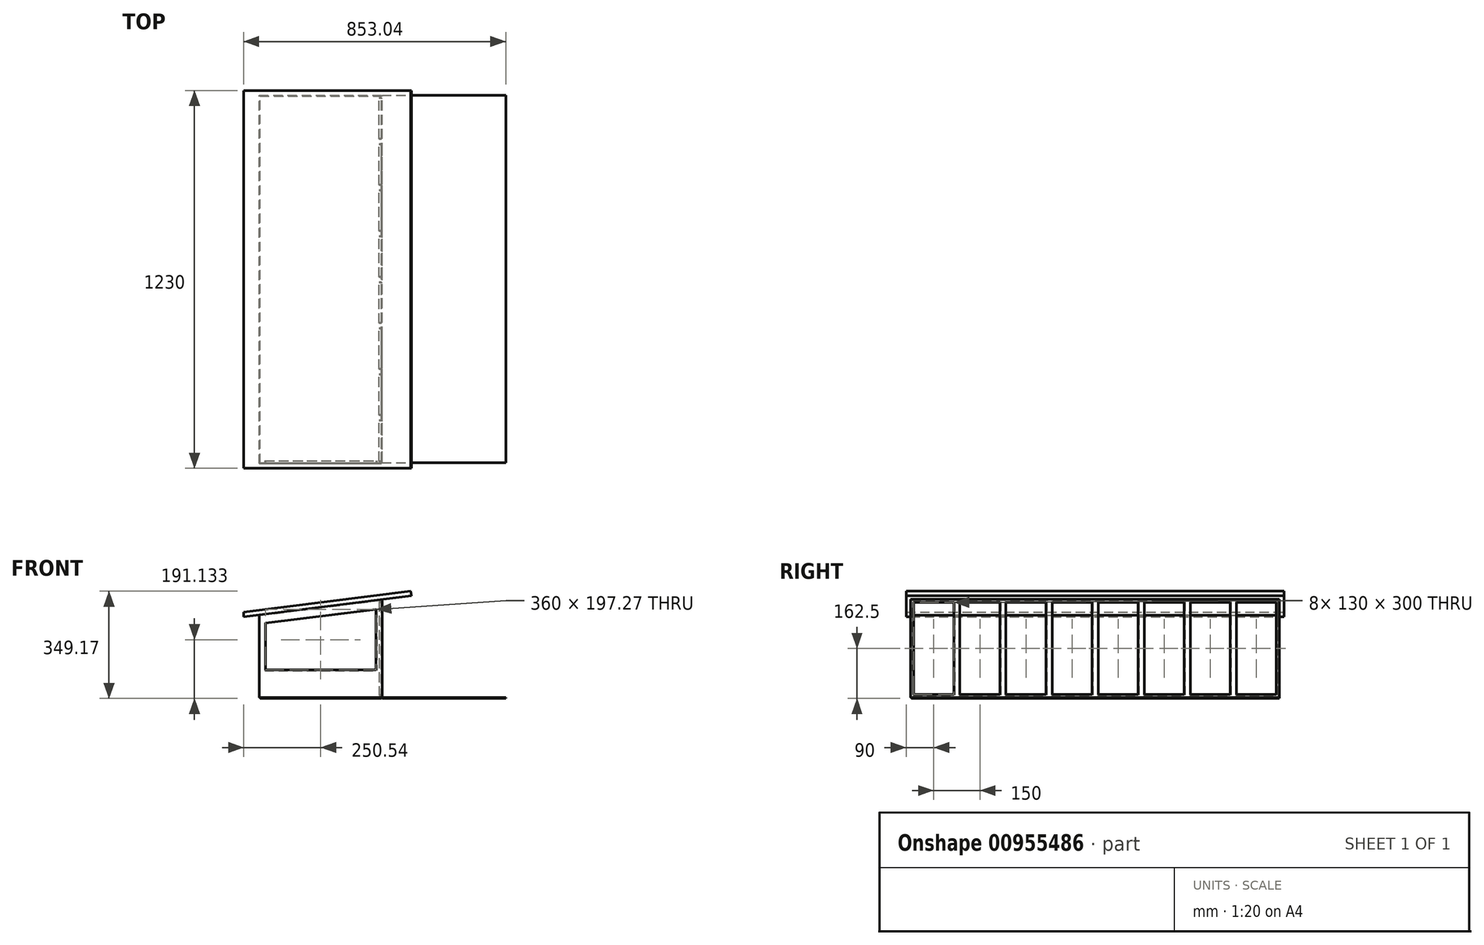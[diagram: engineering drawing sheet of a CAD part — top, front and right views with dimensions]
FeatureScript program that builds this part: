
annotation { "Feature Type Name" : "Feature", "Feature Type Description" : "" }
export const myFeature = defineFeature(function(context is Context, id is Id, definition is map)
    precondition{}
    {
        {
            var Q0;
            Q0=qCreatedBy(makeId("Front.planeOp"),FACE);
            var sketch = newSketch(context, id + "F0", { "sketchPlane" : qUnion([Q0])});
            skLineSegment(sketch, "E0", {"start": v(0, 0) * mm, "end": v(400, 0) * mm});
            skLineSegment(sketch, "E1", {"start": v(0, 0) * mm, "end": v(0, 270) * mm});
            skLineSegment(sketch, "E2", {"start": v(400, 0) * mm, "end": v(400, 320) * mm});
            skLineSegment(sketch, "E3", {"start": v(0, 270) * mm, "end": v(400, 320) * mm});
            skSolve(sketch);
        }
        {
            var Q0;
            Q0 = qSketchRegion(id + "F0", true);
            extrude(context, id + "F1", {"entities" : qUnion([Q0]), "depth" : 1200 * mm, "offsetDistance" : 25 * mm});
        }
        {
            var Q0;
            Q0=qCreatedBy(makeId("Front.planeOp"),FACE);
            var sketch = newSketch(context, id + "F2", { "sketchPlane" : qUnion([Q0])});
            skLineSegment(sketch, "E4", {"start": v(-50.54, 263.68) * mm, "end": v(-50.54, 278.68) * mm});
            skLineSegment(sketch, "E5", {"start": v(-50.54, 278.68) * mm, "end": v(493.37, 346.67) * mm});
            skLineSegment(sketch, "E6", {"start": v(493.37, 346.67) * mm, "end": v(495.22, 331.9) * mm});
            skLineSegment(sketch, "E7", {"start": v(-50.54, 263.68) * mm, "end": v(495.22, 331.9) * mm});
            skSolve(sketch);
        }
        {
            var Q0;
            Q0=makeQuery(id+"F2.imprint","IMPRINT",FACE,{"disambiguationData":[TD([[makeQuery(id+"F2.imprint","IMPRINT",EDGE,{"derivedFrom":sQuery(id+"F2.wireOp",EDGE,"E4")}),-1.0]])]});
            extrude(context, id + "F3", {"entities" : qUnion([Q0]), "depth" : 1215 * mm, "offsetDistance" : 25 * mm, "hasSecondDirection" : true, "secondDirectionOppositeDirection" : true, "secondDirectionDepth" : 15 * mm});
        }
        {
            var Q0;
            Q0=makeQuery(id+"F1.opExtrude","SWEPT_FACE",FACE,{"disambiguationData":[OSD([sQuery(id+"F0.wireOp",EDGE,"E2")])]});
            var sketch = newSketch(context, id + "F4", { "sketchPlane" : qUnion([Q0])});
            skLineSegment(sketch, "E8", {"start": v(-600, 320) * mm, "end": v(-600, 0) * mm});
            skLineSegment(sketch, "E9", {"start": v(-450, 320) * mm, "end": v(-450, 0) * mm});
            skLineSegment(sketch, "E10", {"start": v(-300, 320) * mm, "end": v(-300, 0) * mm});
            skLineSegment(sketch, "E11", {"start": v(-150, 320) * mm, "end": v(-150, 0) * mm});
            skLineSegment(sketch, "E12", {"start": v(-750, 320) * mm, "end": v(-750, 0) * mm});
            skLineSegment(sketch, "E13", {"start": v(-900, 320) * mm, "end": v(-900, 0) * mm});
            skLineSegment(sketch, "E14", {"start": v(-1050, 320) * mm, "end": v(-1050, 0) * mm});
            skLineSegment(sketch, "E15", {"start": v(-1200, 320) * mm, "end": v(-1050, 320) * mm});
            skLineSegment(sketch, "E16", {"start": v(-1050, 320) * mm, "end": v(-900, 320) * mm});
            skLineSegment(sketch, "E17", {"start": v(-900, 320) * mm, "end": v(-750, 320) * mm});
            skLineSegment(sketch, "E18", {"start": v(-750, 320) * mm, "end": v(-600, 320) * mm});
            skLineSegment(sketch, "E19", {"start": v(-600, 320) * mm, "end": v(-450, 320) * mm});
            skLineSegment(sketch, "E20", {"start": v(-450, 320) * mm, "end": v(-300, 320) * mm});
            skLineSegment(sketch, "E21", {"start": v(-300, 320) * mm, "end": v(-150, 320) * mm});
            skLineSegment(sketch, "E22", {"start": v(-150, 320) * mm, "end": v(0, 320) * mm});
            skLineSegment(sketch, "E23.bottom", {"start": v(-1190, 310) * mm, "end": v(-1060, 310) * mm});
            skLineSegment(sketch, "E23.top", {"start": v(-1190, 10) * mm, "end": v(-1060, 10) * mm});
            skLineSegment(sketch, "E23.left", {"start": v(-1190, 310) * mm, "end": v(-1190, 10) * mm});
            skLineSegment(sketch, "E23.right", {"start": v(-1060, 310) * mm, "end": v(-1060, 10) * mm});
            skLineSegment(sketch, "E24.bottom", {"start": v(-1040, 310) * mm, "end": v(-910, 310) * mm});
            skLineSegment(sketch, "E24.top", {"start": v(-1040, 10) * mm, "end": v(-910, 10) * mm});
            skLineSegment(sketch, "E24.left", {"start": v(-1040, 310) * mm, "end": v(-1040, 10) * mm});
            skLineSegment(sketch, "E24.right", {"start": v(-910, 310) * mm, "end": v(-910, 10) * mm});
            skLineSegment(sketch, "E25.bottom", {"start": v(-890, 310) * mm, "end": v(-760, 310) * mm});
            skLineSegment(sketch, "E25.top", {"start": v(-890, 10) * mm, "end": v(-760, 10) * mm});
            skLineSegment(sketch, "E25.left", {"start": v(-890, 310) * mm, "end": v(-890, 10) * mm});
            skLineSegment(sketch, "E25.right", {"start": v(-760, 310) * mm, "end": v(-760, 10) * mm});
            skLineSegment(sketch, "E26.bottom", {"start": v(-740, 310) * mm, "end": v(-610, 310) * mm});
            skLineSegment(sketch, "E26.top", {"start": v(-740, 10) * mm, "end": v(-610, 10) * mm});
            skLineSegment(sketch, "E26.left", {"start": v(-740, 310) * mm, "end": v(-740, 10) * mm});
            skLineSegment(sketch, "E26.right", {"start": v(-610, 310) * mm, "end": v(-610, 10) * mm});
            skLineSegment(sketch, "E27.bottom", {"start": v(-590, 310) * mm, "end": v(-460, 310) * mm});
            skLineSegment(sketch, "E27.top", {"start": v(-590, 10) * mm, "end": v(-460, 10) * mm});
            skLineSegment(sketch, "E27.left", {"start": v(-590, 310) * mm, "end": v(-590, 10) * mm});
            skLineSegment(sketch, "E27.right", {"start": v(-460, 310) * mm, "end": v(-460, 10) * mm});
            skLineSegment(sketch, "E28.bottom", {"start": v(-440, 310) * mm, "end": v(-310, 310) * mm});
            skLineSegment(sketch, "E28.top", {"start": v(-440, 10) * mm, "end": v(-310, 10) * mm});
            skLineSegment(sketch, "E28.left", {"start": v(-440, 310) * mm, "end": v(-440, 10) * mm});
            skLineSegment(sketch, "E28.right", {"start": v(-310, 310) * mm, "end": v(-310, 10) * mm});
            skLineSegment(sketch, "E29.bottom", {"start": v(-290, 310) * mm, "end": v(-160, 310) * mm});
            skLineSegment(sketch, "E29.top", {"start": v(-290, 10) * mm, "end": v(-160, 10) * mm});
            skLineSegment(sketch, "E29.left", {"start": v(-290, 310) * mm, "end": v(-290, 10) * mm});
            skLineSegment(sketch, "E29.right", {"start": v(-160, 310) * mm, "end": v(-160, 10) * mm});
            skLineSegment(sketch, "E30.bottom", {"start": v(-140, 310) * mm, "end": v(-10, 310) * mm});
            skLineSegment(sketch, "E30.top", {"start": v(-140, 10) * mm, "end": v(-10, 10) * mm});
            skLineSegment(sketch, "E30.left", {"start": v(-140, 310) * mm, "end": v(-140, 10) * mm});
            skLineSegment(sketch, "E30.right", {"start": v(-10, 310) * mm, "end": v(-10, 10) * mm});
            skSolve(sketch);
        }
        {
            var Q0;
            Q0=makeQuery(id+"F4.imprint","IMPRINT",FACE,{"disambiguationData":[TD([[makeQuery(id+"F4.imprint","IMPRINT",EDGE,{"derivedFrom":sQuery(id+"F4.wireOp",EDGE,"E23.bottom")}),-1.0]])]});
            var Q1;
            Q1=makeQuery(id+"F4.imprint","IMPRINT",FACE,{"disambiguationData":[TD([[makeQuery(id+"F4.imprint","IMPRINT",EDGE,{"derivedFrom":sQuery(id+"F4.wireOp",EDGE,"E24.bottom")}),-1.0]])]});
            var Q2;
            Q2=makeQuery(id+"F4.imprint","IMPRINT",FACE,{"disambiguationData":[TD([[makeQuery(id+"F4.imprint","IMPRINT",EDGE,{"derivedFrom":sQuery(id+"F4.wireOp",EDGE,"E25.bottom")}),-1.0]])]});
            var Q3;
            Q3=makeQuery(id+"F4.imprint","IMPRINT",FACE,{"disambiguationData":[TD([[makeQuery(id+"F4.imprint","IMPRINT",EDGE,{"derivedFrom":sQuery(id+"F4.wireOp",EDGE,"E26.bottom")}),-1.0]])]});
            var Q4;
            Q4=makeQuery(id+"F4.imprint","IMPRINT",FACE,{"disambiguationData":[TD([[makeQuery(id+"F4.imprint","IMPRINT",EDGE,{"derivedFrom":sQuery(id+"F4.wireOp",EDGE,"E27.bottom")}),-1.0]])]});
            var Q5;
            Q5=makeQuery(id+"F4.imprint","IMPRINT",FACE,{"disambiguationData":[TD([[makeQuery(id+"F4.imprint","IMPRINT",EDGE,{"derivedFrom":sQuery(id+"F4.wireOp",EDGE,"E28.bottom")}),-1.0]])]});
            var Q6;
            Q6=makeQuery(id+"F4.imprint","IMPRINT",FACE,{"disambiguationData":[TD([[makeQuery(id+"F4.imprint","IMPRINT",EDGE,{"derivedFrom":sQuery(id+"F4.wireOp",EDGE,"E29.bottom")}),-1.0]])]});
            var Q7;
            Q7=makeQuery(id+"F4.imprint","IMPRINT",FACE,{"disambiguationData":[TD([[makeQuery(id+"F4.imprint","IMPRINT",EDGE,{"derivedFrom":sQuery(id+"F4.wireOp",EDGE,"E30.bottom")}),-1.0]])]});
            extrude(context, id + "F5", {"entities" : qUnion([Q0, Q1, Q2, Q3, Q4, Q5, Q6, Q7]), "operationType" : NewBodyOperationType.REMOVE, "oppositeDirection" : true, "depth" : 10 * mm, "offsetDistance" : 25 * mm});
        }
        {
            var Q0;
            Q0=makeQuery(id+"F1.opExtrude","CAP_FACE",FACE,{"disambiguationData":[OSD([sQuery(id+"F0.wireOp",EDGE,"E0"),sQuery(id+"F0.wireOp",EDGE,"E1"),sQuery(id+"F0.wireOp",EDGE,"E2"),sQuery(id+"F0.wireOp",EDGE,"E3")])],"isStart":false});
            var sketch = newSketch(context, id + "F6", { "sketchPlane" : qUnion([Q0])});
            skLineSegment(sketch, "E31.top", {"start": v(20, 90) * mm, "end": v(380, 90) * mm});
            skLineSegment(sketch, "E31.left", {"start": v(20, 242.27) * mm, "end": v(20, 90) * mm});
            skLineSegment(sketch, "E31.right", {"start": v(380, 287.27) * mm, "end": v(380, 90) * mm});
            skLineSegment(sketch, "E32", {"start": v(20, 242.27) * mm, "end": v(380, 287.27) * mm});
            skSolve(sketch);
        }
        {
            var Q0;
            Q0=makeQuery(id+"F6.imprint","IMPRINT",FACE,{"disambiguationData":[TD([[makeQuery(id+"F6.imprint","IMPRINT",EDGE,{"derivedFrom":sQuery(id+"F6.wireOp",EDGE,"E31.top")}),1.0]])]});
            extrude(context, id + "F7", {"entities" : qUnion([Q0]), "operationType" : NewBodyOperationType.REMOVE, "oppositeDirection" : true, "depth" : 10 * mm, "offsetDistance" : 25 * mm});
        }
        {
            var Q0;
            Q0=makeQuery(id+"F1.opExtrude","SWEPT_FACE",FACE,{"disambiguationData":[OSD([sQuery(id+"F0.wireOp",EDGE,"E0")])]});
            var Q1;
            Q1=makeQuery(id+"F5.boolean.opBoolean","COPY",FACE,{"derivedFrom":makeQuery(id+"F5.opExtrude","CAP_FACE",FACE,{"disambiguationData":[OSD([sQuery(id+"F4.wireOp",EDGE,"E26.bottom"),sQuery(id+"F4.wireOp",EDGE,"E26.top"),sQuery(id+"F4.wireOp",EDGE,"E26.left"),sQuery(id+"F4.wireOp",EDGE,"E26.right")])],"isStart":false})});
            var Q2;
            Q2=makeQuery(id+"F5.boolean.opBoolean","COPY",FACE,{"derivedFrom":makeQuery(id+"F5.opExtrude","CAP_FACE",FACE,{"disambiguationData":[OSD([sQuery(id+"F4.wireOp",EDGE,"E27.bottom"),sQuery(id+"F4.wireOp",EDGE,"E27.top"),sQuery(id+"F4.wireOp",EDGE,"E27.left"),sQuery(id+"F4.wireOp",EDGE,"E27.right")])],"isStart":false})});
            var Q3;
            Q3=makeQuery(id+"F5.boolean.opBoolean","COPY",FACE,{"derivedFrom":makeQuery(id+"F5.opExtrude","CAP_FACE",FACE,{"disambiguationData":[OSD([sQuery(id+"F4.wireOp",EDGE,"E28.bottom"),sQuery(id+"F4.wireOp",EDGE,"E28.top"),sQuery(id+"F4.wireOp",EDGE,"E28.left"),sQuery(id+"F4.wireOp",EDGE,"E28.right")])],"isStart":false})});
            var Q4;
            Q4=makeQuery(id+"F5.boolean.opBoolean","COPY",FACE,{"derivedFrom":makeQuery(id+"F5.opExtrude","CAP_FACE",FACE,{"disambiguationData":[OSD([sQuery(id+"F4.wireOp",EDGE,"E29.bottom"),sQuery(id+"F4.wireOp",EDGE,"E29.top"),sQuery(id+"F4.wireOp",EDGE,"E29.left"),sQuery(id+"F4.wireOp",EDGE,"E29.right")])],"isStart":false})});
            var Q5;
            Q5=makeQuery(id+"F5.boolean.opBoolean","COPY",FACE,{"derivedFrom":makeQuery(id+"F5.opExtrude","CAP_FACE",FACE,{"disambiguationData":[OSD([sQuery(id+"F4.wireOp",EDGE,"E30.bottom"),sQuery(id+"F4.wireOp",EDGE,"E30.top"),sQuery(id+"F4.wireOp",EDGE,"E30.left"),sQuery(id+"F4.wireOp",EDGE,"E30.right")])],"isStart":false})});
            var Q6;
            Q6=makeQuery(id+"F5.boolean.opBoolean","COPY",FACE,{"derivedFrom":makeQuery(id+"F5.opExtrude","CAP_FACE",FACE,{"disambiguationData":[OSD([sQuery(id+"F4.wireOp",EDGE,"E25.bottom"),sQuery(id+"F4.wireOp",EDGE,"E25.top"),sQuery(id+"F4.wireOp",EDGE,"E25.left"),sQuery(id+"F4.wireOp",EDGE,"E25.right")])],"isStart":false})});
            var Q7;
            Q7=makeQuery(id+"F5.boolean.opBoolean","COPY",FACE,{"derivedFrom":makeQuery(id+"F5.opExtrude","CAP_FACE",FACE,{"disambiguationData":[OSD([sQuery(id+"F4.wireOp",EDGE,"E24.bottom"),sQuery(id+"F4.wireOp",EDGE,"E24.top"),sQuery(id+"F4.wireOp",EDGE,"E24.left"),sQuery(id+"F4.wireOp",EDGE,"E24.right")])],"isStart":false})});
            var Q8;
            Q8=makeQuery(id+"F5.boolean.opBoolean","COPY",FACE,{"derivedFrom":makeQuery(id+"F5.opExtrude","CAP_FACE",FACE,{"disambiguationData":[OSD([sQuery(id+"F4.wireOp",EDGE,"E23.bottom"),sQuery(id+"F4.wireOp",EDGE,"E23.top"),sQuery(id+"F4.wireOp",EDGE,"E23.left"),sQuery(id+"F4.wireOp",EDGE,"E23.right")])],"isStart":false})});
            var Q9;
            Q9=makeQuery(id+"F7.boolean.opBoolean","COPY",FACE,{"derivedFrom":makeQuery(id+"F7.opExtrude","CAP_FACE",FACE,{"disambiguationData":[OSD([sQuery(id+"F6.wireOp",EDGE,"E31.top"),sQuery(id+"F6.wireOp",EDGE,"E31.left"),sQuery(id+"F6.wireOp",EDGE,"E31.right"),sQuery(id+"F6.wireOp",EDGE,"E32")])],"isStart":false})});
            shell(context, id + "F8", {"entities" : qUnion([Q0, Q1, Q2, Q3, Q4, Q5, Q6, Q7, Q8, Q9]), "thickness" : 2.5 * mm});
        }
        {
            var Q0;
            Q0=makeQuery(id+"F1.opExtrude","SWEPT_FACE",FACE,{"disambiguationData":[OSD([sQuery(id+"F0.wireOp",EDGE,"E0")])]});
            var sketch = newSketch(context, id + "F9", { "sketchPlane" : qUnion([Q0])});
            skLineSegment(sketch, "E33.bottom", {"start": v(2.5, 1197.5) * mm, "end": v(802.5, 1197.5) * mm});
            skLineSegment(sketch, "E33.top", {"start": v(2.5, 0) * mm, "end": v(802.5, 0) * mm});
            skLineSegment(sketch, "E33.left", {"start": v(2.5, 1197.5) * mm, "end": v(2.5, 0) * mm});
            skLineSegment(sketch, "E33.right", {"start": v(802.5, 1197.5) * mm, "end": v(802.5, 0) * mm});
            skSolve(sketch);
        }
        {
            var Q0;
            {var subQ0=sQuery(id+"F9.wireOp",EDGE,"E33.right");Q0=makeQuery(id+"F9.imprint","IMPRINT",FACE,{"disambiguationData":[TD([[makeQuery(id+"F9.imprint","IMPRINT",EDGE,{"derivedFrom":subQ0}),-1.0]])]});}
            var Q1;
            {var subQ3=sQuery(id+"F0.wireOp",EDGE,"E0");var subQ5=makeQuery(id+"F8.opShell","OFFSET_EDGE",EDGE,{"disambiguationData":[OSD([subQ3]),TDD([makeQuery(id+"F1.opExtrude","CAP_EDGE",EDGE,{"disambiguationData":[OSD([subQ3])],"isStart":true})])]});Q1=makeQuery(id+"F9.imprint","IMPRINT",FACE,{"disambiguationData":[TD([[makeQuery(id+"F9.imprint","IMPRINT",EDGE,{"derivedFrom":subQ5}),1.0]])]});}
            extrude(context, id + "F10", {"entities" : qUnion([Q0, Q1]), "depth" : 2.5 * mm, "offsetDistance" : 25 * mm});
        }
    });
